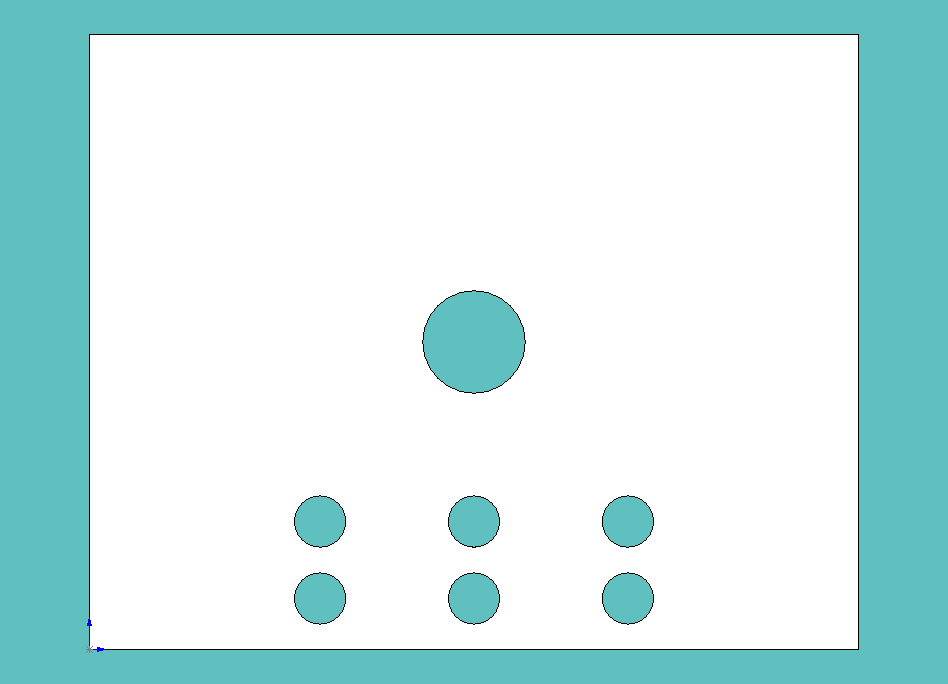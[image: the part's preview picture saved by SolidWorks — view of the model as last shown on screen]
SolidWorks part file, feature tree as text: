
SOLIDWORKS PART (.sldprt)
format: sldprt  version: not decoded by parser v0  size: 178,688 bytes
history: native  units: mm
features: plane x3, sketch x3, cut_extrude x2, pattern_linear x2, material x1, extrude x1 (+8 scaffold rows collapsed)
feature tree (20):
  scaffold x8  (default folders/planes/origin — collapsed)
  material  "Matériau <non spécifié>"
  plane  "Plan de face"
  plane  "Plan de dessus"
  plane  "Plan de droite"
  sketch  "Esquisse1"  dims[D1=120.0mm D2=150.0mm]
  extrude  "Extrusion1"  Depth=5mm
  sketch  "Esquisse2"  dims[D1=~11.438373mm]
  cut_extrude  "Enlèv. mat.-Extru.1"  Depth=10mm
  sketch  "Esquisse3"  dims[D1=10.0mm D2=10.0mm D3=45.0mm]
  cut_extrude  "Enlèv. mat.-Extru.2"  Depth=10mm
  pattern_linear  "Répétition linéaire1"  Count1=3 Count2=1 Spacing1=30mm Spacing2=50mm
  pattern_linear  "Répétition linéaire2"  Count1=2 Count2=1 Spacing1=15mm Spacing2=50mm
decode coverage: 8 of 8 modeling features carry decoded parameters
note: ~ marks probable driven/reference dimensions
note: suppression state not decoded; provenance and decode notes live in map.json
